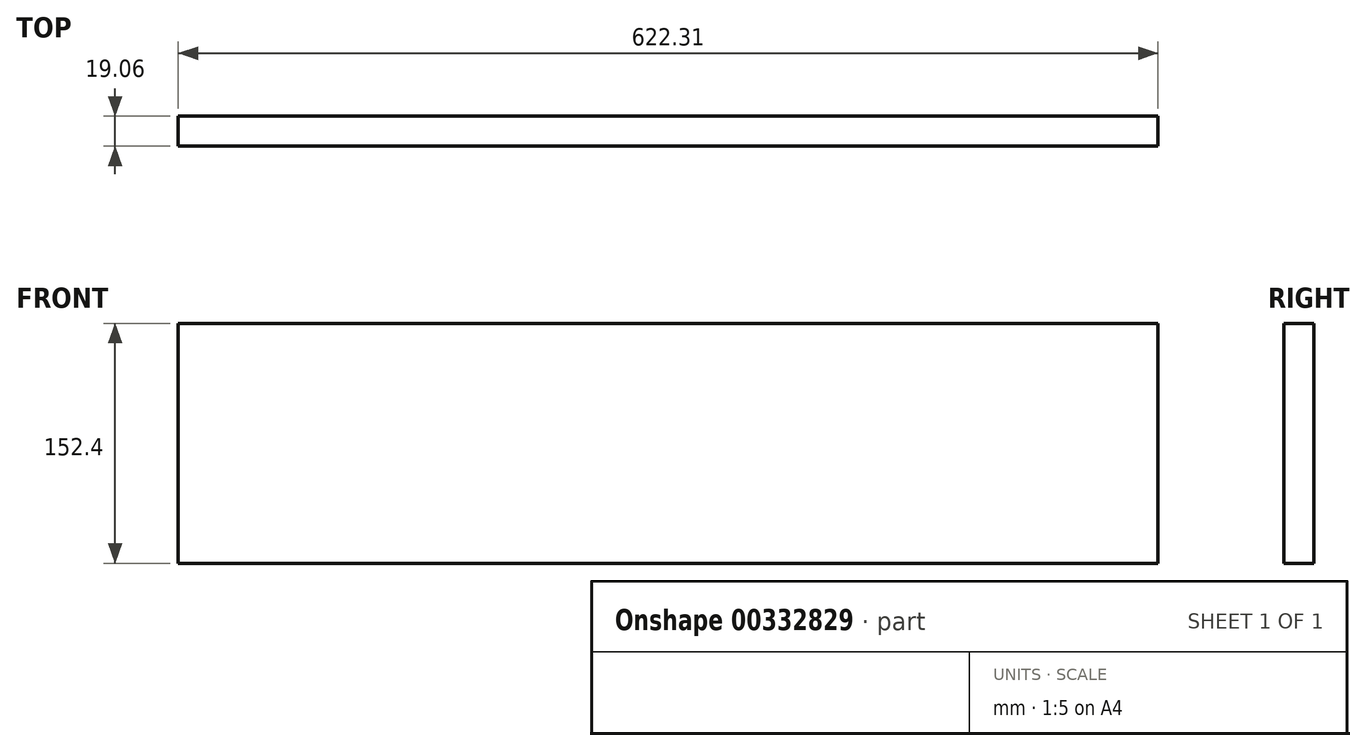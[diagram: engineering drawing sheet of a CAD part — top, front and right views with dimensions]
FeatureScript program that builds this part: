
annotation { "Feature Type Name" : "Feature", "Feature Type Description" : "" }
export const myFeature = defineFeature(function(context is Context, id is Id, definition is map)
    precondition{}
    {
        {
            var Q0;
            Q0=qCreatedBy(makeId("Top.planeOp"),FACE);
            var sketch = newSketch(context, id + "F0", { "sketchPlane" : qUnion([Q0])});
            skLineSegment(sketch, "E0.bottom", {"start": v(-60.32, -9.53) * mm, "end": v(561.98, -9.53) * mm});
            skLineSegment(sketch, "E0.top", {"start": v(-60.32, 9.52) * mm, "end": v(561.98, 9.52) * mm});
            skLineSegment(sketch, "E0.right", {"start": v(561.98, -9.53) * mm, "end": v(561.98, 9.52) * mm});
            skPoint(sketch, "E0.middle", {"position": v(0, 0) * mm});
            skPoint(sketch, "E0.left.end.orphan", {"position": v(-561.98, 9.52) * mm});
            skPoint(sketch, "E1.start.orphan", {"position": v(-561.98, -9.53) * mm});
            skLineSegment(sketch, "E2", {"start": v(-60.32, 9.52) * mm, "end": v(-60.32, -9.53) * mm});
            skSolve(sketch);
        }
        {
            var Q0;
            Q0=qSketchRegion(id+"F0",true);
            extrude(context, id + "F1", {"entities" : qUnion([Q0]), "depth" : 152.4 * mm});
        }
    });
